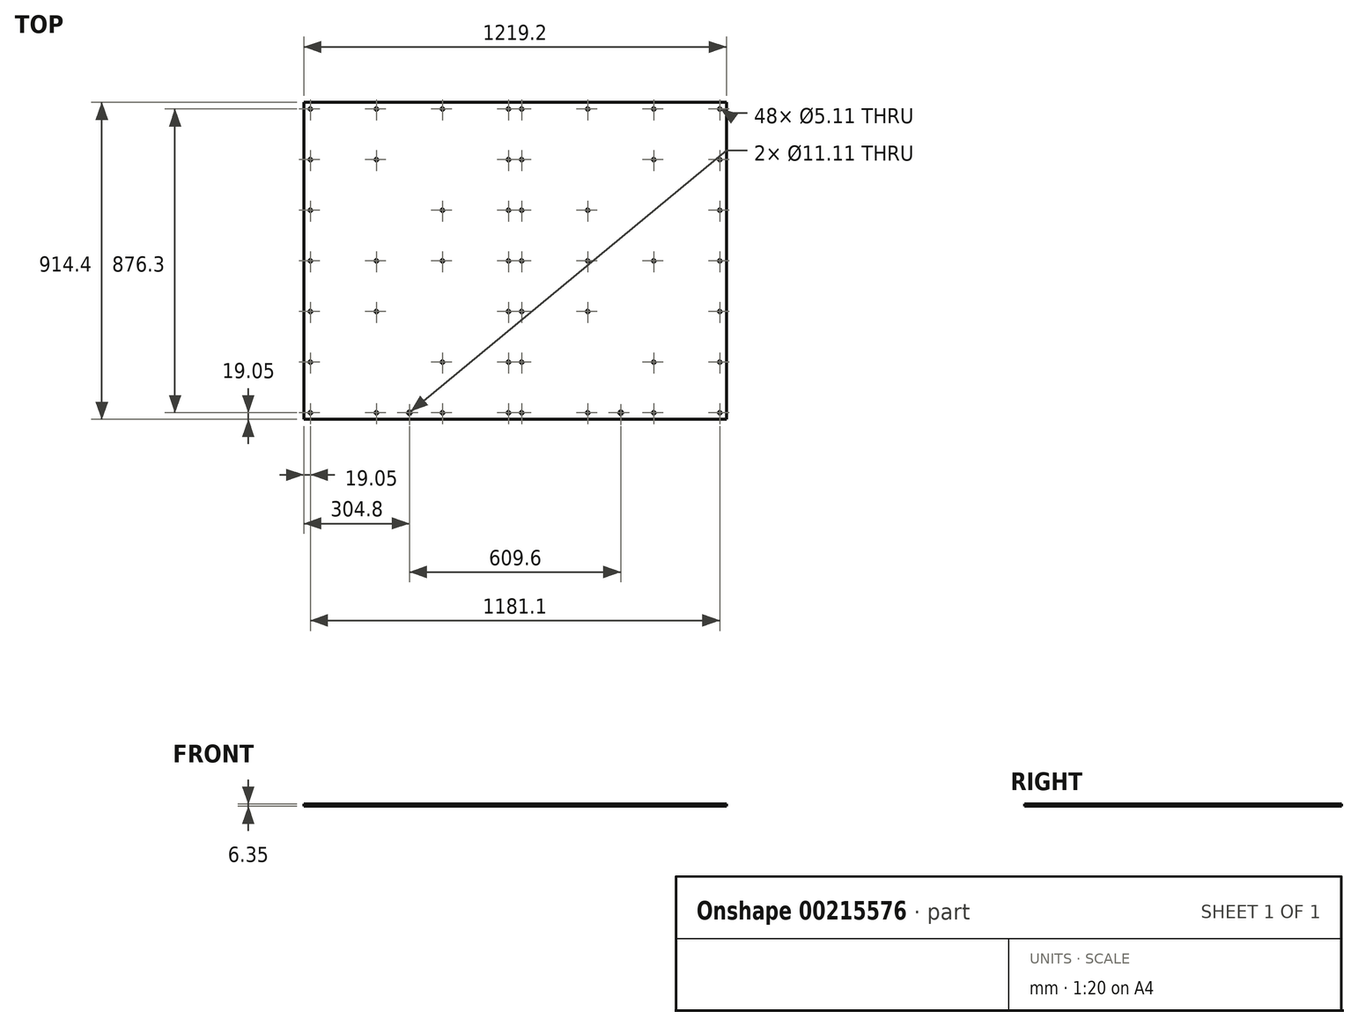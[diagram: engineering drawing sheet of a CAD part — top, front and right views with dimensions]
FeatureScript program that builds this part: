
annotation { "Feature Type Name" : "Feature", "Feature Type Description" : "" }
export const myFeature = defineFeature(function(context is Context, id is Id, definition is map)
    precondition{}
    {
        {
            var Q0;
            Q0=qCreatedBy(makeId("Top.planeOp"),FACE);
            var sketch = newSketch(context, id + "F0", { "sketchPlane" : qUnion([Q0])});
            skLineSegment(sketch, "E0.bottom", {"start": v(609.6, 457.2) * mm, "end": v(-609.6, 457.2) * mm});
            skLineSegment(sketch, "E0.top", {"start": v(609.6, -457.2) * mm, "end": v(-609.6, -457.2) * mm});
            skLineSegment(sketch, "E0.left", {"start": v(609.6, 457.2) * mm, "end": v(609.6, -457.2) * mm});
            skLineSegment(sketch, "E0.right", {"start": v(-609.6, 457.2) * mm, "end": v(-609.6, -457.2) * mm});
            skPoint(sketch, "E0.middle", {"position": v(0, 0) * mm});
            skSolve(sketch);
        }
        {
            var Q0;
            Q0=makeQuery(id+"F0.imprint","IMPRINT",FACE,{"disambiguationData":[TD([[makeQuery(id+"F0.imprint","IMPRINT",EDGE,{"derivedFrom":sQuery(id+"F0.wireOp",EDGE,"E0.bottom")}),1.0]])]});
            extrude(context, id + "F1", {"entities" : qUnion([Q0]), "depth" : 6.35 * mm});
        }
        {
            var Q0;
            Q0=makeQuery(id+"F1.opExtrude","CAP_FACE",FACE,{"disambiguationData":[OSD([sQuery(id+"F0.wireOp",EDGE,"E0.bottom"),sQuery(id+"F0.wireOp",EDGE,"E0.top"),sQuery(id+"F0.wireOp",EDGE,"E0.left"),sQuery(id+"F0.wireOp",EDGE,"E0.right")])],"isStart":false});
            var sketch = newSketch(context, id + "F2", { "sketchPlane" : qUnion([Q0])});
            skPoint(sketch, "E1", {"position": v(-590.55, 438.15) * mm});
            skPoint(sketch, "E2", {"position": v(590.55, 438.15) * mm});
            skPoint(sketch, "E3.0.1.0", {"position": v(-590.55, 292.1) * mm});
            skPoint(sketch, "E3.0.2.0", {"position": v(-590.55, 146.05) * mm});
            skPoint(sketch, "E3.0.3.0", {"position": v(-590.55, 0) * mm});
            skPoint(sketch, "E3.0.4.0", {"position": v(-590.55, -146.05) * mm});
            skPoint(sketch, "E3.0.5.0", {"position": v(-590.55, -292.1) * mm});
            skPoint(sketch, "E3.1.0.0", {"position": v(-400.05, 438.15) * mm});
            skPoint(sketch, "E3.1.1.0", {"position": v(-400.05, 292.1) * mm});
            skPoint(sketch, "E3.1.3.0", {"position": v(-400.05, 0) * mm});
            skPoint(sketch, "E3.1.4.0", {"position": v(-400.05, -146.05) * mm});
            skPoint(sketch, "E3.2.0.0", {"position": v(-209.55, 438.15) * mm});
            skPoint(sketch, "E3.2.2.0", {"position": v(-209.55, 146.05) * mm});
            skPoint(sketch, "E3.2.3.0", {"position": v(-209.55, 0) * mm});
            skPoint(sketch, "E3.2.5.0", {"position": v(-209.55, -292.1) * mm});
            skPoint(sketch, "E3.3.0.0", {"position": v(-19.05, 438.15) * mm});
            skPoint(sketch, "E3.3.1.0", {"position": v(-19.05, 292.1) * mm});
            skPoint(sketch, "E3.3.2.0", {"position": v(-19.05, 146.05) * mm});
            skPoint(sketch, "E3.3.3.0", {"position": v(-19.05, 0) * mm});
            skPoint(sketch, "E3.3.4.0", {"position": v(-19.05, -146.05) * mm});
            skPoint(sketch, "E3.3.5.0", {"position": v(-19.05, -292.1) * mm});
            skLineSegment(sketch, "E3.direction1", {"start": v(-590.55, 438.15) * mm, "end": v(-400.05, 438.15) * mm, "construction": true});
            skLineSegment(sketch, "E3.direction2", {"start": v(-590.55, 438.15) * mm, "end": v(-590.55, 292.1) * mm, "construction": true});
            skPoint(sketch, "E4.0.1.0", {"position": v(590.55, 292.1) * mm});
            skPoint(sketch, "E4.0.2.0", {"position": v(590.55, 146.05) * mm});
            skPoint(sketch, "E4.0.3.0", {"position": v(590.55, 0) * mm});
            skPoint(sketch, "E4.0.4.0", {"position": v(590.55, -146.05) * mm});
            skPoint(sketch, "E4.0.5.0", {"position": v(590.55, -292.1) * mm});
            skPoint(sketch, "E4.1.0.0", {"position": v(400.05, 438.15) * mm});
            skPoint(sketch, "E4.1.1.0", {"position": v(400.05, 292.1) * mm});
            skPoint(sketch, "E4.1.3.0", {"position": v(400.05, 0) * mm});
            skPoint(sketch, "E4.1.5.0", {"position": v(400.05, -292.1) * mm});
            skPoint(sketch, "E4.2.0.0", {"position": v(209.55, 438.15) * mm});
            skPoint(sketch, "E4.2.2.0", {"position": v(209.55, 146.05) * mm});
            skPoint(sketch, "E4.2.3.0", {"position": v(209.55, 0) * mm});
            skPoint(sketch, "E4.2.4.0", {"position": v(209.55, -146.05) * mm});
            skPoint(sketch, "E4.3.0.0", {"position": v(19.05, 438.15) * mm});
            skPoint(sketch, "E4.3.1.0", {"position": v(19.05, 292.1) * mm});
            skPoint(sketch, "E4.3.2.0", {"position": v(19.05, 146.05) * mm});
            skPoint(sketch, "E4.3.3.0", {"position": v(19.05, 0) * mm});
            skPoint(sketch, "E4.3.4.0", {"position": v(19.05, -146.05) * mm});
            skPoint(sketch, "E4.3.5.0", {"position": v(19.05, -292.1) * mm});
            skLineSegment(sketch, "E4.direction1", {"start": v(590.55, 438.15) * mm, "end": v(400.05, 438.15) * mm, "construction": true});
            skLineSegment(sketch, "E4.direction2", {"start": v(590.55, 438.15) * mm, "end": v(590.55, 292.1) * mm, "construction": true});
            skPoint(sketch, "E5.0.0.6", {"position": v(590.55, -438.15) * mm});
            skPoint(sketch, "E5.0.1.6", {"position": v(400.05, -438.15) * mm});
            skPoint(sketch, "E5.0.2.6", {"position": v(209.55, -438.15) * mm});
            skPoint(sketch, "E5.0.3.6", {"position": v(19.05, -438.15) * mm});
            skPoint(sketch, "E6.0.0.6", {"position": v(-590.55, -438.15) * mm});
            skPoint(sketch, "E6.0.1.6", {"position": v(-400.05, -438.15) * mm});
            skPoint(sketch, "E6.0.2.6", {"position": v(-209.55, -438.15) * mm});
            skPoint(sketch, "E6.0.3.6", {"position": v(-19.05, -438.15) * mm});
            skPoint(sketch, "E7", {"position": v(304.8, -438.15) * mm});
            skPoint(sketch, "E8", {"position": v(-304.8, -438.15) * mm});
            skSolve(sketch);
        }
        {
            var Q0;
            Q0=sQuery(id+"F2.wireOp",VERTEX,"E1");
            var Q1;
            Q1=sQuery(id+"F2.wireOp",VERTEX,"E3.1.0.0");
            var Q2;
            Q2=sQuery(id+"F2.wireOp",VERTEX,"E3.2.0.0");
            var Q3;
            Q3=sQuery(id+"F2.wireOp",VERTEX,"E3.3.0.0");
            var Q4;
            Q4=sQuery(id+"F2.wireOp",VERTEX,"E4.3.0.0");
            var Q5;
            Q5=sQuery(id+"F2.wireOp",VERTEX,"E4.2.0.0");
            var Q6;
            Q6=sQuery(id+"F2.wireOp",VERTEX,"E4.1.0.0");
            var Q7;
            Q7=sQuery(id+"F2.wireOp",VERTEX,"E2");
            var Q8;
            Q8=sQuery(id+"F2.wireOp",VERTEX,"E4.0.1.0");
            var Q9;
            Q9=sQuery(id+"F2.wireOp",VERTEX,"E4.0.2.0");
            var Q10;
            Q10=sQuery(id+"F2.wireOp",VERTEX,"E4.0.3.0");
            var Q11;
            Q11=sQuery(id+"F2.wireOp",VERTEX,"E4.0.4.0");
            var Q12;
            Q12=sQuery(id+"F2.wireOp",VERTEX,"E4.0.5.0");
            var Q13;
            Q13=sQuery(id+"F2.wireOp",VERTEX,"E5.0.0.6");
            var Q14;
            Q14=sQuery(id+"F2.wireOp",VERTEX,"E5.0.1.6");
            var Q15;
            Q15=sQuery(id+"F2.wireOp",VERTEX,"E5.0.2.6");
            var Q16;
            Q16=sQuery(id+"F2.wireOp",VERTEX,"E5.0.3.6");
            var Q17;
            Q17=sQuery(id+"F2.wireOp",VERTEX,"E6.0.3.6");
            var Q18;
            Q18=sQuery(id+"F2.wireOp",VERTEX,"E6.0.2.6");
            var Q19;
            Q19=sQuery(id+"F2.wireOp",VERTEX,"E6.0.1.6");
            var Q20;
            Q20=sQuery(id+"F2.wireOp",VERTEX,"E6.0.0.6");
            var Q21;
            Q21=sQuery(id+"F2.wireOp",VERTEX,"E3.0.5.0");
            var Q22;
            Q22=sQuery(id+"F2.wireOp",VERTEX,"E3.0.4.0");
            var Q23;
            Q23=sQuery(id+"F2.wireOp",VERTEX,"E3.0.3.0");
            var Q24;
            Q24=sQuery(id+"F2.wireOp",VERTEX,"E3.0.2.0");
            var Q25;
            Q25=sQuery(id+"F2.wireOp",VERTEX,"E3.0.1.0");
            var Q26;
            Q26=sQuery(id+"F2.wireOp",VERTEX,"E3.3.5.0");
            var Q27;
            Q27=sQuery(id+"F2.wireOp",VERTEX,"E4.3.5.0");
            var Q28;
            Q28=sQuery(id+"F2.wireOp",VERTEX,"E3.3.4.0");
            var Q29;
            Q29=sQuery(id+"F2.wireOp",VERTEX,"E4.3.4.0");
            var Q30;
            Q30=sQuery(id+"F2.wireOp",VERTEX,"E3.3.3.0");
            var Q31;
            Q31=sQuery(id+"F2.wireOp",VERTEX,"E4.3.3.0");
            var Q32;
            Q32=sQuery(id+"F2.wireOp",VERTEX,"E3.3.2.0");
            var Q33;
            Q33=sQuery(id+"F2.wireOp",VERTEX,"E4.3.2.0");
            var Q34;
            Q34=sQuery(id+"F2.wireOp",VERTEX,"E3.3.1.0");
            var Q35;
            Q35=sQuery(id+"F2.wireOp",VERTEX,"E4.3.1.0");
            var Q36;
            Q36=sQuery(id+"F2.wireOp",VERTEX,"E3.1.1.0");
            var Q37;
            Q37=sQuery(id+"F2.wireOp",VERTEX,"E3.1.3.0");
            var Q38;
            Q38=sQuery(id+"F2.wireOp",VERTEX,"E3.1.4.0");
            var Q39;
            Q39=sQuery(id+"F2.wireOp",VERTEX,"E3.2.5.0");
            var Q40;
            Q40=sQuery(id+"F2.wireOp",VERTEX,"E3.2.3.0");
            var Q41;
            Q41=sQuery(id+"F2.wireOp",VERTEX,"E3.2.2.0");
            var Q42;
            Q42=sQuery(id+"F2.wireOp",VERTEX,"E4.2.2.0");
            var Q43;
            Q43=sQuery(id+"F2.wireOp",VERTEX,"E4.2.3.0");
            var Q44;
            Q44=sQuery(id+"F2.wireOp",VERTEX,"E4.2.4.0");
            var Q45;
            Q45=sQuery(id+"F2.wireOp",VERTEX,"E4.1.5.0");
            var Q46;
            Q46=sQuery(id+"F2.wireOp",VERTEX,"E4.1.3.0");
            var Q47;
            Q47=sQuery(id+"F2.wireOp",VERTEX,"E4.1.1.0");
            var Q48;
            Q48=makeQuery(id+"F1.opExtrude","SWEPT_BODY",BODY,{"disambiguationData":[OSD([sQuery(id+"F0.wireOp",EDGE,"E0.bottom"),sQuery(id+"F0.wireOp",EDGE,"E0.top"),sQuery(id+"F0.wireOp",EDGE,"E0.left"),sQuery(id+"F0.wireOp",EDGE,"E0.right")])]});
            hole(context, id + "F3", {"style" : HoleStyle.C_SINK, "endStyle" : HoleEndStyle.THROUGH, "holeDiameter" : 5.1 * mm, "cSinkDiameter" : 7.94 * mm, "cSinkAngle" : 82 * degree, "locations" : qUnion([Q0, Q1, Q2, Q3, Q4, Q5, Q6, Q7, Q8, Q9, Q10, Q11, Q12, Q13, Q14, Q15, Q16, Q17, Q18, Q19, Q20, Q21, Q22, Q23, Q24, Q25, Q26, Q27, Q28, Q29, Q30, Q31, Q32, Q33, Q34, Q35, Q36, Q37, Q38, Q39, Q40, Q41, Q42, Q43, Q44, Q45, Q46, Q47]), "scope" : qUnion([Q48]), "isTappedThrough" : true});
        }
        {
            var Q0;
            Q0=sQuery(id+"F2.wireOp",VERTEX,"E7");
            var Q1;
            Q1=sQuery(id+"F2.wireOp",VERTEX,"E8");
            var Q2;
            Q2=makeQuery(id+"F1.opExtrude","SWEPT_BODY",BODY,{"disambiguationData":[OSD([sQuery(id+"F0.wireOp",EDGE,"E0.bottom"),sQuery(id+"F0.wireOp",EDGE,"E0.top"),sQuery(id+"F0.wireOp",EDGE,"E0.left"),sQuery(id+"F0.wireOp",EDGE,"E0.right")])]});
            hole(context, id + "F4", {"style" : HoleStyle.SIMPLE, "endStyle" : HoleEndStyle.THROUGH, "holeDiameter" : 11.1 * mm, "locations" : qUnion([Q0, Q1]), "scope" : qUnion([Q2]), "isTappedThrough" : true});
        }
    });
